# Revit family: 318_2452047480c84a5db376201c8469e4
name_source: partatom
category: Pipe Accessories
units: mm (PartAtom-declared; Revit-internal decimal feet)

## family parameters
Always vertical = Yes
Cut with Voids When Loaded = No
Part Type = Valve - Normal
Round Connector Dimension = Use Diameter
Shared = No
Work Plane-Based = No

## types (1)
- FAR-3827 11409
    B = 45 mm  [stored 0.147638 ft]
    B1 = 8 mm  [stored 0.0262467 ft]
    B1__ve = -8 mm  [stored -0.0262467 ft]
    B2 = 6 mm  [stored 0.019685 ft]
    B2__ve = -6 mm
    B3 = 4 mm  [stored 0.0131234 ft]
    B4 = 27 mm
    BP = 25 mm
    C = 70 mm
    C1 = 35 mm
    CAT0 = Yes
    CenSd_R_6 = 23 mm
    Description = 1"1/4 Brass modular manifold m-f, 9 ports M33x1,5
    E1 = 39 mm
    E1__ve = -39 mm
    E2 = 4 mm  [stored 0.0131234 ft]
    E2__ve = -4 mm
    E3 = 17 mm  [stored 0.0557743 ft]
    E3__ve = -17 mm  [stored -0.0557743 ft]
    L = 642 mm  [stored 2.1063 ft]
    L1 = 15 mm  [stored 0.0492126 ft]
    L1__ve = -15 mm  [stored -0.0492126 ft]
    L3 = 627 mm  [stored 2.05709 ft]
    L3__ve = -627 mm  [stored -2.05709 ft]
    L4 = 10 mm  [stored 0.0328084 ft]
    L4__ve = -10 mm  [stored -0.0328084 ft]
    L5 = 314 mm
    L6 = 8 mm  [stored 0.0262467 ft]
    MP1 = 32 mm
    MP2 = 32 mm
    Manufacturer = FAR
    QmdConnectorList = 301;MP1;302;MP2;303;BP;304;BP;305;BP;306;BP;307;BP;308;BP;309;BP;310;BP;311;BP
    R = 26 mm  [stored 0.0853018 ft]
    R1 = 16 mm  [stored 0.0524934 ft]
    R10 = 18 mm
    R11 = 17 mm  [stored 0.0557743 ft]
    R13 = 10 mm  [stored 0.0328084 ft]
    R14 = 20 mm  [stored 0.0656168 ft]
    R14__ve = -20 mm  [stored -0.0656168 ft]
    R15 = 17 mm  [stored 0.0557743 ft]
    R4 = 13 mm
    R8 = 16 mm  [stored 0.0524934 ft]
    R9 = 15 mm  [stored 0.0492126 ft]
    URL = www.far.eu
    magiPartTypeId = 318
    magiProductCode = FAR-3827 11409
    magiProductFamilyId = 2452047480c84a5db376201c8469e4
    magiProductId = 2452047480c84a5db376201c8469e4

note: [stored X ft] marks values corroborated as IEEE doubles in the binary element streams (Revit-internal decimal feet)

## geometry (parser evidence)
native form markers: Sweep x3
no freeform markers — native parametric forms only
